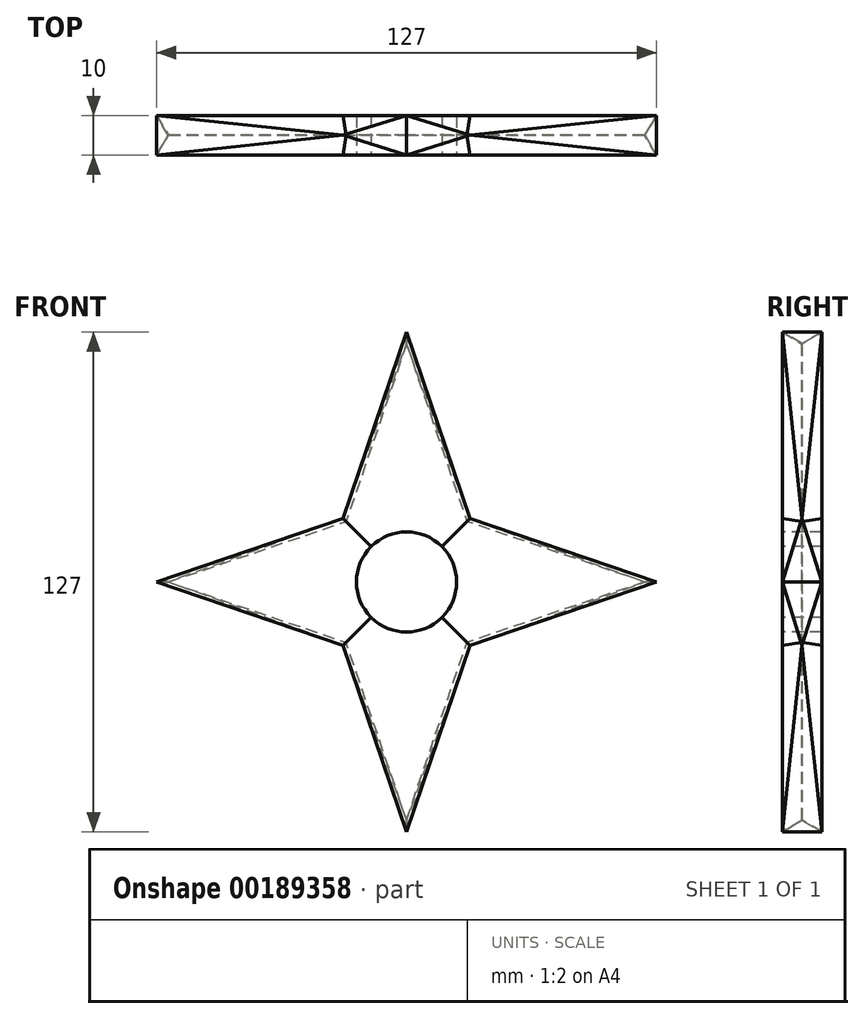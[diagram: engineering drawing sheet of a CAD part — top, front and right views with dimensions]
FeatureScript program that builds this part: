
annotation { "Feature Type Name" : "Feature", "Feature Type Description" : "" }
export const myFeature = defineFeature(function(context is Context, id is Id, definition is map)
    precondition{}
    {
        {
            var Q0;
            Q0=qCreatedBy(makeId("Front.planeOp"),FACE);
            var sketch = newSketch(context, id + "F0", { "sketchPlane" : qUnion([Q0])});
            skLineSegment(sketch, "E0", {"start": v(0, 68.4) * mm, "end": v(0, -68.4) * mm, "construction": true});
            skLineSegment(sketch, "E1", {"start": v(-81.02, 0) * mm, "end": v(82.15, 0) * mm, "construction": true});
            skLineSegment(sketch, "E2", {"start": v(-16.11, 16.11) * mm, "end": v(-63.5, 0) * mm});
            skLineSegment(sketch, "E3", {"start": v(-16.11, 16.11) * mm, "end": v(0, 0) * mm});
            skLineSegment(sketch, "E4", {"start": v(-63.5, 0) * mm, "end": v(0, 0) * mm});
            skLineSegment(sketch, "E5", {"start": v(0, 63.5) * mm, "end": v(0, 0) * mm});
            skSolve(sketch);
        }
        {
            var Q0;
            Q0 = qSketchRegion(id + "F0", true);
            extrude(context, id + "F1", {"entities" : qUnion([Q0]), "depth" : 5 * mm});
        }
        {
            var Q0;
            Q0=makeQuery(id+"F1.opExtrude","SWEPT_FACE",FACE,{"disambiguationData":[OSD([sQuery(id+"F0.wireOp",EDGE,"E4")])]});
            var sketch = newSketch(context, id + "F2", { "sketchPlane" : qUnion([Q0])});
            skLineSegment(sketch, "E6", {"start": v(-63.5, 5) * mm, "end": v(0, 5) * mm});
            skLineSegment(sketch, "E7", {"start": v(0, 5) * mm, "end": v(-63.5, 0) * mm});
            skLineSegment(sketch, "E8", {"start": v(-63.5, 0) * mm, "end": v(-63.5, 5) * mm});
            skSolve(sketch);
        }
        {
            var Q0;
            Q0=makeQuery(id+"F1.opExtrude","SWEPT_FACE",FACE,{"disambiguationData":[OSD([sQuery(id+"F0.wireOp",EDGE,"E3")])]});
            var sketch = newSketch(context, id + "F3", { "sketchPlane" : qUnion([Q0])});
            skLineSegment(sketch, "E9", {"start": v(0, -5) * mm, "end": v(-22.79, 0) * mm});
            skSolve(sketch);
        }
        {
            var Q0;
            Q0 = qSketchRegion(id + "F2", true);
            var Q1;
            Q1 = qConstructionFilter(qBodyType(qCreatedBy(id + "F3" ,EDGE), BodyType.WIRE), ConstructionObject.NO);
            sweep(context, id + "F4", {"operationType" : NewBodyOperationType.REMOVE, "profiles" : qUnion([Q0]), "path" : qUnion([Q1])});
        }
        {
            var Q0;
            {var subQ1=sQuery(id+"F0.wireOp",EDGE,"E2");Q0=makeQuery(id+"F4.boolean.opBoolean","SPLIT",FACE,{"disambiguationData":[TD([makeQuery(id+"F4.opSweep","SWEPT_FACE",FACE,{"disambiguationData":[OSD([sQuery(id+"F2.wireOp",EDGE,"E6"),sQuery(id+"F3.wireOp",EDGE,"S3P1vj80-u9lD-UfN3-08U2-v9NZqPo1Lj9m")])]})])],"derivedFrom":makeQuery(id+"F1.opExtrude","SWEPT_FACE",FACE,{"disambiguationData":[OSD([subQ1])]})});}
            var sketch = newSketch(context, id + "F5", { "sketchPlane" : qUnion([Q0])});
            skLineSegment(sketch, "E10.0.0", {"start": v(-10.07, -5) * mm, "end": v(-10.07, 0) * mm});
            skLineSegment(sketch, "E10.0.1", {"start": v(-10.07, 0) * mm, "end": v(-60.12, -5) * mm});
            skLineSegment(sketch, "E10.0.2", {"start": v(-60.12, -5) * mm, "end": v(-10.07, -5) * mm});
            skSolve(sketch);
        }
        {
            var Q0;
            Q0 = qSketchRegion(id + "F5", true);
            var Q1;
            Q1 = qConstructionFilter(qBodyType(qCreatedBy(id + "F3" ,EDGE), BodyType.WIRE), ConstructionObject.NO);
            sweep(context, id + "F6", {"operationType" : NewBodyOperationType.REMOVE, "profiles" : qUnion([Q0]), "path" : qUnion([Q1])});
        }
        {
            var Q0;
            Q0=makeQuery(id+"F4.boolean.opBoolean","SPLIT",BODY,{"disambiguationData":[OD(0.0)],"derivedFrom":makeQuery(id+"F1.opExtrude","SWEPT_BODY",BODY,{"disambiguationData":[OSD([sQuery(id+"F0.wireOp",EDGE,"E2"),sQuery(id+"F0.wireOp",EDGE,"E3"),sQuery(id+"F0.wireOp",EDGE,"E4")])]})});
            var Q1;
            Q1=qCreatedBy(makeId("Top.planeOp"),FACE);
            mirror(context, id + "F7", {"operationType" : NewBodyOperationType.ADD, "entities" : qUnion([Q0]), "mirrorPlane" : qUnion([Q1])});
        }
        {
            var Q0;
            Q0=makeQuery(id+"F4.boolean.opBoolean","SPLIT",BODY,{"disambiguationData":[OD(0.0)],"derivedFrom":makeQuery(id+"F1.opExtrude","SWEPT_BODY",BODY,{"disambiguationData":[OSD([sQuery(id+"F0.wireOp",EDGE,"E2"),sQuery(id+"F0.wireOp",EDGE,"E3"),sQuery(id+"F0.wireOp",EDGE,"E4")])]})});
            var Q1;
            Q1=qCreatedBy(makeId("Front.planeOp"),FACE);
            mirror(context, id + "F8", {"operationType" : NewBodyOperationType.ADD, "entities" : qUnion([Q0]), "mirrorPlane" : qUnion([Q1])});
        }
        {
            var Q0;
            Q0=qCreatedBy(makeId("Top.planeOp"),FACE);
            var sketch = newSketch(context, id + "F9", { "sketchPlane" : qUnion([Q0])});
            skLineSegment(sketch, "E11", {"start": v(0, -46.27) * mm, "end": v(0, 54.71) * mm, "construction": true});
            skSolve(sketch);
        }
        {
            var Q0;
            Q0=makeQuery(id+"F4.boolean.opBoolean","SPLIT",BODY,{"disambiguationData":[OD(0.0)],"derivedFrom":makeQuery(id+"F1.opExtrude","SWEPT_BODY",BODY,{"disambiguationData":[OSD([sQuery(id+"F0.wireOp",EDGE,"E2"),sQuery(id+"F0.wireOp",EDGE,"E3"),sQuery(id+"F0.wireOp",EDGE,"E4")])]})});
            var Q1;
            Q1=sQuery(id+"F9.wireOp",EDGE,"E11");
            circularPattern(context, id + "F10", {"entities" : qUnion([Q0]), "axis" : qUnion([Q1]), "angle" : 90 * degree, "instanceCount" : 4});
        }
        {
            var Q0;
            Q0=qCreatedBy(makeId("Front.planeOp"),FACE);
            var sketch = newSketch(context, id + "F11", { "sketchPlane" : qUnion([Q0])});
            skCircle(sketch, "E12", {"center": v(0, 0) * mm, "radius": 12.7 * mm});
            skSolve(sketch);
        }
        {
            var Q0;
            Q0 = qSketchRegion(id + "F11", true);
            extrude(context, id + "F12", {"entities" : qUnion([Q0]), "operationType" : NewBodyOperationType.REMOVE, "endBound" : BoundingType.SYMMETRIC, "oppositeDirection" : true, "depth" : 25.4 * mm});
        }
    });
